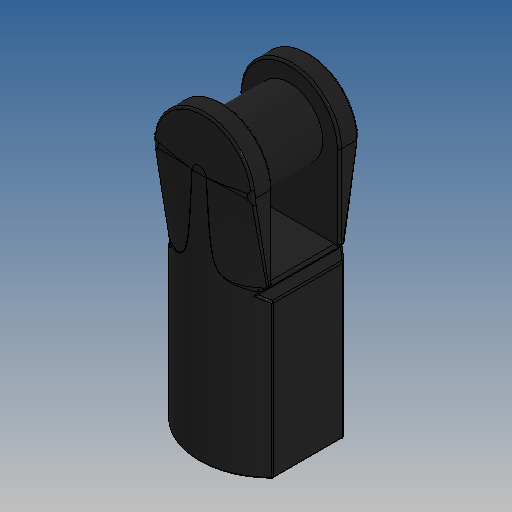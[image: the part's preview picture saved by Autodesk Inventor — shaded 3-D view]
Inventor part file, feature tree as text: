
AUTODESK INVENTOR PART (.ipt)
format: ipt  version: 2025 (Build 290162010, 162A)  size: 734,208 bytes
history: native  units: in
note: dims shown in document units (in); Inventor stores cm internally (conversion verified against a paired STEP export)
features: sketch x9, extrude x6, loft x2, plane x1, revolve x1, mirror x1, fillet x1
ambient origin geometry x8: Origin, YZ Plane, XZ Plane, XY Plane, X Axis, Y Axis, Z Axis, Center Point
bodies: Solid1 (feature_tree)
feature tree (21):
  extrude  "Extrusion1"  Depth=0.2161in
  sketch  "Sketch5"  dims[d3=0.1969in d4=0.4724in d5=0.0in]
  sketch  "Sketch12"  dims[d25=0.0671in d26=0.189in]
  sketch  "Sketch13"  dims[d27=0.063in d42=0.189in]
  plane  "Work Plane1"
  sketch  "Sketch7"  dims[d11=-0.1819in d19=0.063in]
  sketch  "Sketch14"  dims[d43=0.0998in d44=0.189in]
  loft  "Loft3"
  loft  "Loft4"
  revolve  "Revolution3"  [1 undecoded]
  mirror  "Mirror1"
  sketch  "Sketch11"  dims[d21=0.189in d23=0.0998in]
  extrude  "Extrusion2"  Depth=0.189in
  extrude  "Extrusion3"  Depth=0.189in
  extrude  "Extrusion4"  Depth=0.189in
  extrude  "Extrusion5"  TaperAngle=0.0deg  [1 undecoded]
  extrude  "Extrusion6"  Depth=0.1575in
  fillet  "Fillet1"  Radius=0.126in
  sketch  "Sketch2"  dims[d1=0.1378in d2=0.2161in]
  sketch  "Sketch15"  dims[d45=0.0998in d48=0.0in d49=90.0deg d58=0.0in d59=90.0deg]
  sketch  "Sketch16"  dims[d60=180.0deg d61=0.1575in d62=0.126in d63=0.2906in d64=0.3211in d65=0.3in d66=0.1644in d67=0.315in d68=0.0in d69=0.315in d70=0.0in d71=0.315in d72=0.0in d73=0.0in d74=90.0deg d75=0.0in d76=90.0deg d77=0.126in d78=0.1575in d79=0.0in d80=0.063in d81=0.2205in d82=0.0984in d83=0.0in d84=0.0039in d85=0.0787in]
note: 2 required parameter values undecoded (feature->parameter linkage not recoverable at this tier; creation-order binding heuristic only, values carry confidence <= 0.55)